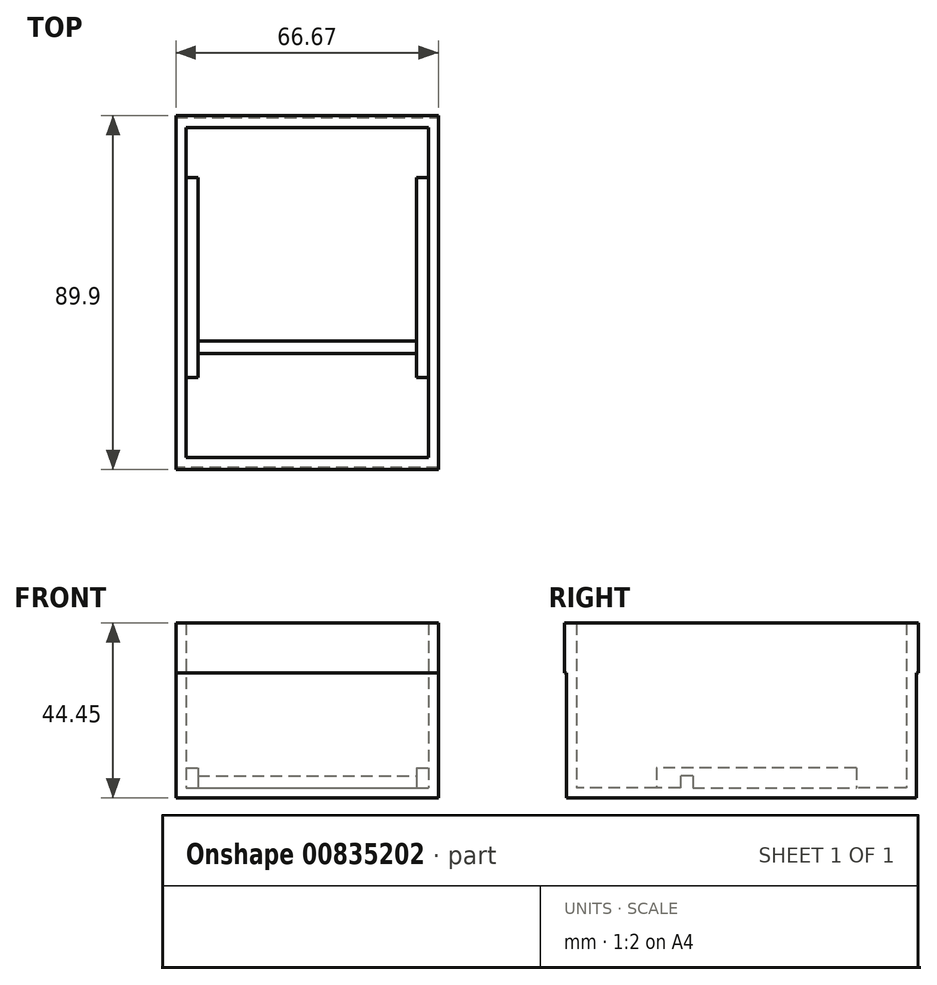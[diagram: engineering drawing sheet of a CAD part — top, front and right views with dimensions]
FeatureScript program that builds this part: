
annotation { "Feature Type Name" : "Feature", "Feature Type Description" : "" }
export const myFeature = defineFeature(function(context is Context, id is Id, definition is map)
    precondition{}
    {
        {
            var Q0;
            Q0=qCreatedBy(makeId("Top.planeOp"),FACE);
            var sketch = newSketch(context, id + "F0", { "sketchPlane" : qUnion([Q0])});
            skLineSegment(sketch, "E0.bottom", {"start": v(-34.46, 55.3) * mm, "end": v(32.21, 55.3) * mm});
            skLineSegment(sketch, "E0.top", {"start": v(-34.46, -33.6) * mm, "end": v(32.21, -33.6) * mm});
            skLineSegment(sketch, "E0.left", {"start": v(-34.46, 55.3) * mm, "end": v(-34.46, -33.6) * mm});
            skLineSegment(sketch, "E0.right", {"start": v(32.21, 55.3) * mm, "end": v(32.21, -33.6) * mm});
            skSolve(sketch);
        }
        {
            var Q0;
            Q0=makeQuery(id+"F0.imprint","IMPRINT",FACE,{"disambiguationData":[TD([[makeQuery(id+"F0.imprint","IMPRINT",EDGE,{"derivedFrom":sQuery(id+"F0.wireOp",EDGE,"E0.bottom")}),-1.0]])]});
            extrude(context, id + "F1", {"entities" : qUnion([Q0]), "depth" : 44.45 * mm, "offsetDistance" : 25.4 * mm});
        }
        {
            var Q0;
            Q0=makeQuery(id+"F1.opExtrude","CAP_FACE",FACE,{"disambiguationData":[OSD([sQuery(id+"F0.wireOp",EDGE,"E0.bottom"),sQuery(id+"F0.wireOp",EDGE,"E0.top"),sQuery(id+"F0.wireOp",EDGE,"E0.left"),sQuery(id+"F0.wireOp",EDGE,"E0.right")])],"isStart":false});
            shell(context, id + "F2", {"entities" : qUnion([Q0]), "thickness" : 2.54 * mm});
        }
        {
            var Q0;
            Q0=makeQuery(id+"F2.opShell","OFFSET_FACE",FACE,{"disambiguationData":[OSD([sQuery(id+"F0.wireOp",EDGE,"E0.bottom"),sQuery(id+"F0.wireOp",EDGE,"E0.top"),sQuery(id+"F0.wireOp",EDGE,"E0.left"),sQuery(id+"F0.wireOp",EDGE,"E0.right")])]});
            var sketch = newSketch(context, id + "F3", { "sketchPlane" : qUnion([Q0])});
            skLineSegment(sketch, "E1", {"start": v(-31.92, 40.07) * mm, "end": v(29.67, 40.07) * mm});
            skLineSegment(sketch, "E2", {"start": v(-31.92, -10.73) * mm, "end": v(29.67, -10.73) * mm});
            skLineSegment(sketch, "E3", {"start": v(26.63, 40.07) * mm, "end": v(26.63, -10.73) * mm});
            skLineSegment(sketch, "E4", {"start": v(-28.87, -10.73) * mm, "end": v(-28.87, 40.07) * mm});
            skLineSegment(sketch, "E5", {"start": v(-28.87, -1.46) * mm, "end": v(26.63, -1.46) * mm});
            skLineSegment(sketch, "E6", {"start": v(-28.87, -4.64) * mm, "end": v(26.63, -4.64) * mm});
            skSolve(sketch);
        }
        {
            var Q0;
            {var subQ4=sQuery(id+"F3.wireOp",EDGE,"E3");Q0=makeQuery(id+"F3.imprint","IMPRINT",FACE,{"disambiguationData":[TD([[makeQuery(id+"F3.imprint","IMPRINT",EDGE,{"derivedFrom":subQ4}),1.0]])]});}
            var Q1;
            {var subQ4=sQuery(id+"F3.wireOp",EDGE,"E4");Q1=makeQuery(id+"F3.imprint","IMPRINT",FACE,{"disambiguationData":[TD([[makeQuery(id+"F3.imprint","IMPRINT",EDGE,{"derivedFrom":subQ4}),1.0]])]});}
            extrude(context, id + "F4", {"entities" : qUnion([Q0, Q1]), "operationType" : NewBodyOperationType.ADD, "depth" : 5.08 * mm, "offsetDistance" : 25.4 * mm});
        }
        {
            var Q0;
            {var subQ0=sQuery(id+"F3.wireOp",EDGE,"E5");Q0=makeQuery(id+"F3.imprint","IMPRINT",FACE,{"disambiguationData":[TD([[makeQuery(id+"F3.imprint","IMPRINT",EDGE,{"derivedFrom":subQ0}),-1.0]])]});}
            extrude(context, id + "F5", {"entities" : qUnion([Q0]), "operationType" : NewBodyOperationType.ADD, "depth" : 3.05 * mm, "offsetDistance" : 25.4 * mm});
        }
        {
            var Q0;
            Q0=makeQuery(id+"F1.opExtrude","SWEPT_FACE",FACE,{"disambiguationData":[OSD([sQuery(id+"F0.wireOp",EDGE,"E0.bottom")])]});
            var sketch = newSketch(context, id + "F6", { "sketchPlane" : qUnion([Q0])});
            skLineSegment(sketch, "E7.bottom", {"start": v(34.46, 44.45) * mm, "end": v(-32.21, 44.45) * mm});
            skLineSegment(sketch, "E7.top", {"start": v(34.46, 31.75) * mm, "end": v(-32.21, 31.75) * mm});
            skLineSegment(sketch, "E7.left", {"start": v(34.46, 44.45) * mm, "end": v(34.46, 31.75) * mm});
            skLineSegment(sketch, "E7.right", {"start": v(-32.21, 44.45) * mm, "end": v(-32.21, 31.75) * mm});
            skSolve(sketch);
        }
        {
            var Q0;
            Q0=makeQuery(id+"F6.imprint","IMPRINT",FACE,{"disambiguationData":[TD([[makeQuery(id+"F6.imprint","IMPRINT",EDGE,{"derivedFrom":sQuery(id+"F6.wireOp",EDGE,"E7.bottom")}),1.0]])]});
            extrude(context, id + "F7", {"entities" : qUnion([Q0]), "operationType" : NewBodyOperationType.ADD, "depth" : .5 * mm, "offsetDistance" : 25.4 * mm});
        }
        {
            var Q0;
            Q0=makeQuery(id+"F1.opExtrude","SWEPT_FACE",FACE,{"disambiguationData":[OSD([sQuery(id+"F0.wireOp",EDGE,"E0.top")])]});
            var sketch = newSketch(context, id + "F8", { "sketchPlane" : qUnion([Q0])});
            skLineSegment(sketch, "E8.bottom", {"start": v(32.21, 44.45) * mm, "end": v(-34.46, 44.45) * mm});
            skLineSegment(sketch, "E8.top", {"start": v(32.21, 31.75) * mm, "end": v(-34.46, 31.75) * mm});
            skLineSegment(sketch, "E8.left", {"start": v(32.21, 44.45) * mm, "end": v(32.21, 31.75) * mm});
            skLineSegment(sketch, "E8.right", {"start": v(-34.46, 44.45) * mm, "end": v(-34.46, 31.75) * mm});
            skSolve(sketch);
        }
        {
            var Q0;
            Q0=makeQuery(id+"F8.imprint","IMPRINT",FACE,{"disambiguationData":[TD([[makeQuery(id+"F8.imprint","IMPRINT",EDGE,{"derivedFrom":sQuery(id+"F8.wireOp",EDGE,"E8.bottom")}),-1.0]])]});
            extrude(context, id + "F9", {"entities" : qUnion([Q0]), "operationType" : NewBodyOperationType.ADD, "depth" : .5 * mm, "offsetDistance" : 25.4 * mm});
        }
    });
